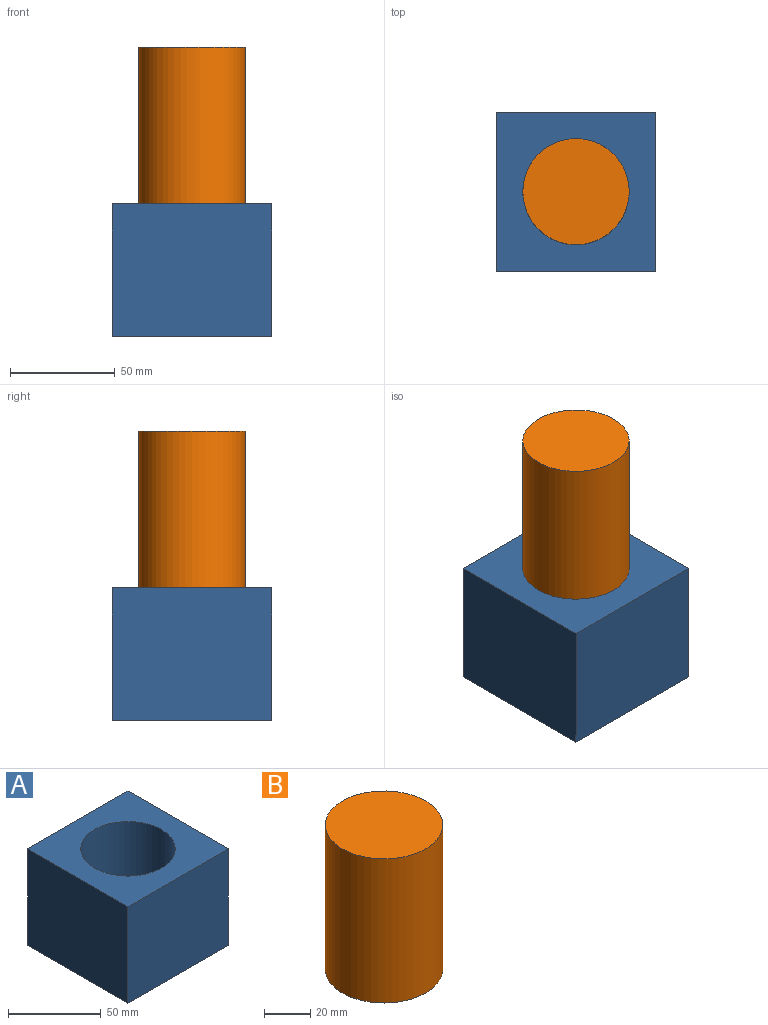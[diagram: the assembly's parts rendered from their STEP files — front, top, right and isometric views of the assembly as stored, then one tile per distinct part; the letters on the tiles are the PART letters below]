
ASSEMBLY  parts=2 mates=1
PART A: 8 faces, bbox 76.2x76.2x63.5 mm
  f0: plane 76.2x63.5mm, normal (1,0,0), area 4838.7mm2, adj f1,f3,f5,f7
  f1: plane 76.2x63.5mm, normal (0,1,0), area 4838.7mm2, adj f0,f2,f5,f7
  f2: plane 76.2x63.5mm, normal (-1,0,0), area 4838.7mm2, adj f1,f3,f5,f7
  f3: plane 76.2x63.5mm, normal (0,-1,0), area 4838.7mm2, adj f0,f2,f5,f7
  f4: cylinder r=25.4mm len=50.8mm, axis (0,0,-1), area 6080.5mm2, adj f5,f6
  f5: plane 76.2x76.2mm, normal (0,0,1), area 3779.6mm2, adj f0,f1,f2,f3,f4
  f6: plane 50.8x50.8mm, normal (0,0,1), area 2026.8mm2, adj f4
  f7: plane 76.2x76.2mm, normal (0,0,-1), area 5806.4mm2, adj f0,f1,f2,f3
PART B: 3 faces, bbox 50.8x50.8x76.2 mm
  f0: cylinder r=25.4mm len=76.2mm, axis (0,0,1), area 12161mm2, adj f1,f2
  f1: plane 50.8x50.8mm, normal (0,0,-1), area 2026.8mm2, adj f0
  f2: plane 50.8x50.8mm, normal (0,0,1), area 2026.8mm2, adj f0
PLACE A rot(axis=(0.08,0.93,0.37),0deg) t=(-0.46,-125.2,12.44)mm fixed
PLACE B rot(axis=(0,0,-1),180deg) t=(-0.46,-125.2,138.04)mm
MATE slider B.f0 <-> A.f4  axis (0,0,1) through (-0.46,-125.2,99.94)mm
